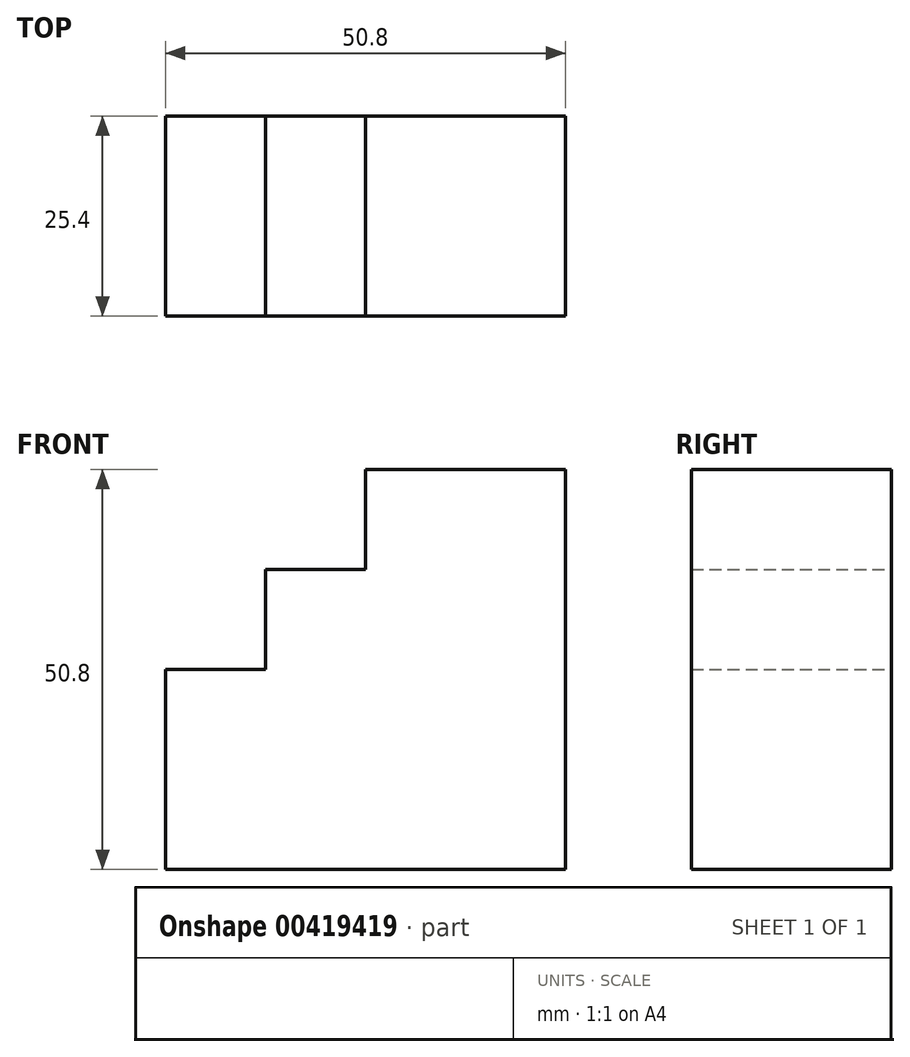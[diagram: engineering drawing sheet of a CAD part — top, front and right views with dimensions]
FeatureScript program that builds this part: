
annotation { "Feature Type Name" : "Feature", "Feature Type Description" : "" }
export const myFeature = defineFeature(function(context is Context, id is Id, definition is map)
    precondition{}
    {
        {
            var Q0;
            Q0=qCreatedBy(makeId("Front.planeOp"),FACE);
            var sketch = newSketch(context, id + "F0", { "sketchPlane" : qUnion([Q0])});
            skLineSegment(sketch, "E0", {"start": v(37.05, 29.6) * mm, "end": v(37.05, -21.2) * mm});
            skLineSegment(sketch, "E1", {"start": v(37.05, 29.6) * mm, "end": v(11.65, 29.6) * mm});
            skLineSegment(sketch, "E2", {"start": v(11.65, 29.6) * mm, "end": v(11.65, 16.9) * mm});
            skLineSegment(sketch, "E3", {"start": v(11.65, 16.9) * mm, "end": v(-1.05, 16.9) * mm});
            skLineSegment(sketch, "E4", {"start": v(-1.05, 16.9) * mm, "end": v(-1.05, 4.2) * mm});
            skLineSegment(sketch, "E5", {"start": v(-1.05, 4.2) * mm, "end": v(-13.75, 4.2) * mm});
            skLineSegment(sketch, "E6", {"start": v(-13.75, 4.2) * mm, "end": v(-13.75, -21.2) * mm});
            skLineSegment(sketch, "E7", {"start": v(-13.75, -21.2) * mm, "end": v(37.05, -21.2) * mm});
            skSolve(sketch);
        }
        {
            var Q0;
            Q0 = qSketchRegion(id + "F0", true);
            extrude(context, id + "F1", {"entities" : qUnion([Q0]), "depth" : 25.4 * mm});
        }
    });
